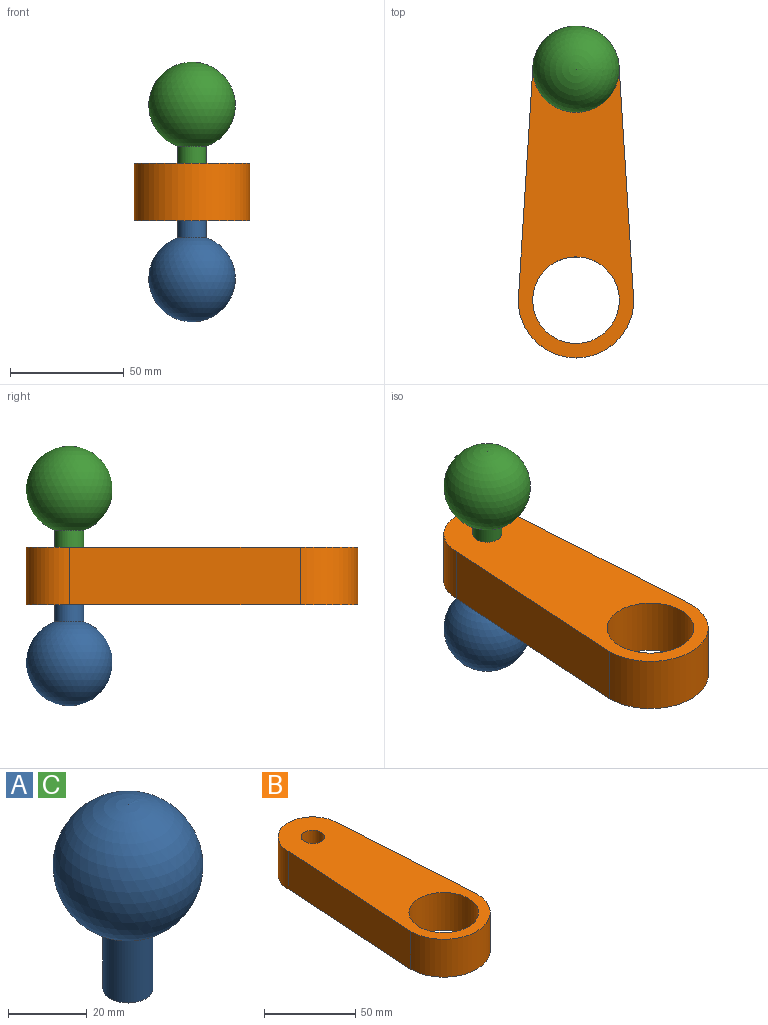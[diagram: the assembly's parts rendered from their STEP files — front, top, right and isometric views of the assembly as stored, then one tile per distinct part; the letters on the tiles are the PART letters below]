
ASSEMBLY  parts=3 mates=2
PART A: 3 faces, bbox 38.1x38.1x57.2 mm
  f0: cylinder r=6.35mm len=20.14mm, axis (0,0,1), area 803.5mm2, adj f1,f2
  f1: plane 12.7x12.7mm, normal (0,0,-1), area 126.7mm2, adj f0
  f2: sphere r=19.05mm, area 4430mm2, adj f0
PART B: 8 faces, bbox 50.8x146.1x25.4 mm
  f0: plane 101.6x25.4mm, normal (-1,0.06,0), area 2585.7mm2, adj f1,f4,f6,f7
  f1: cylinder r=25.4mm len=50.8mm, axis (0,0,-1), area 2026.8mm2, adj f0,f2,f6,f7
  f2: plane 101.6x25.4mm, normal (1,0.06,0), area 2585.7mm2, adj f1,f4,f6,f7
  f3: cylinder r=6.35mm len=25.4mm, axis (0,0,-1), area 1013.4mm2, adj f6,f7
  f4: cylinder r=19.05mm len=38.1mm, axis (0,0,-1), area 1520.1mm2, adj f0,f2,f6,f7
  f5: cylinder r=19.05mm len=38.1mm, axis (0,0,-1), area 3040.2mm2, adj f6,f7
  f6: plane 146.05x50.8mm, normal (0,0,1), area 4832.8mm2, adj f0,f1,f2,f3,f4,f5
  f7: plane 146.05x50.8mm, normal (0,0,-1), area 4832.8mm2, adj f0,f1,f2,f3,f4,f5
PART C: same geometry as A
PLACE A rot(axis=(1,0,0),180deg) t=(0,101.6,-25.4)mm
PLACE B at identity
PLACE C t=(0,101.6,50.8)mm
MATE fastened C.f0 <-> B.f3  axis (0,0,-1) through (0,101.6,12.7)mm
MATE fastened A.f0 <-> B.f3  axis (0,0,1) through (0,101.6,12.7)mm
